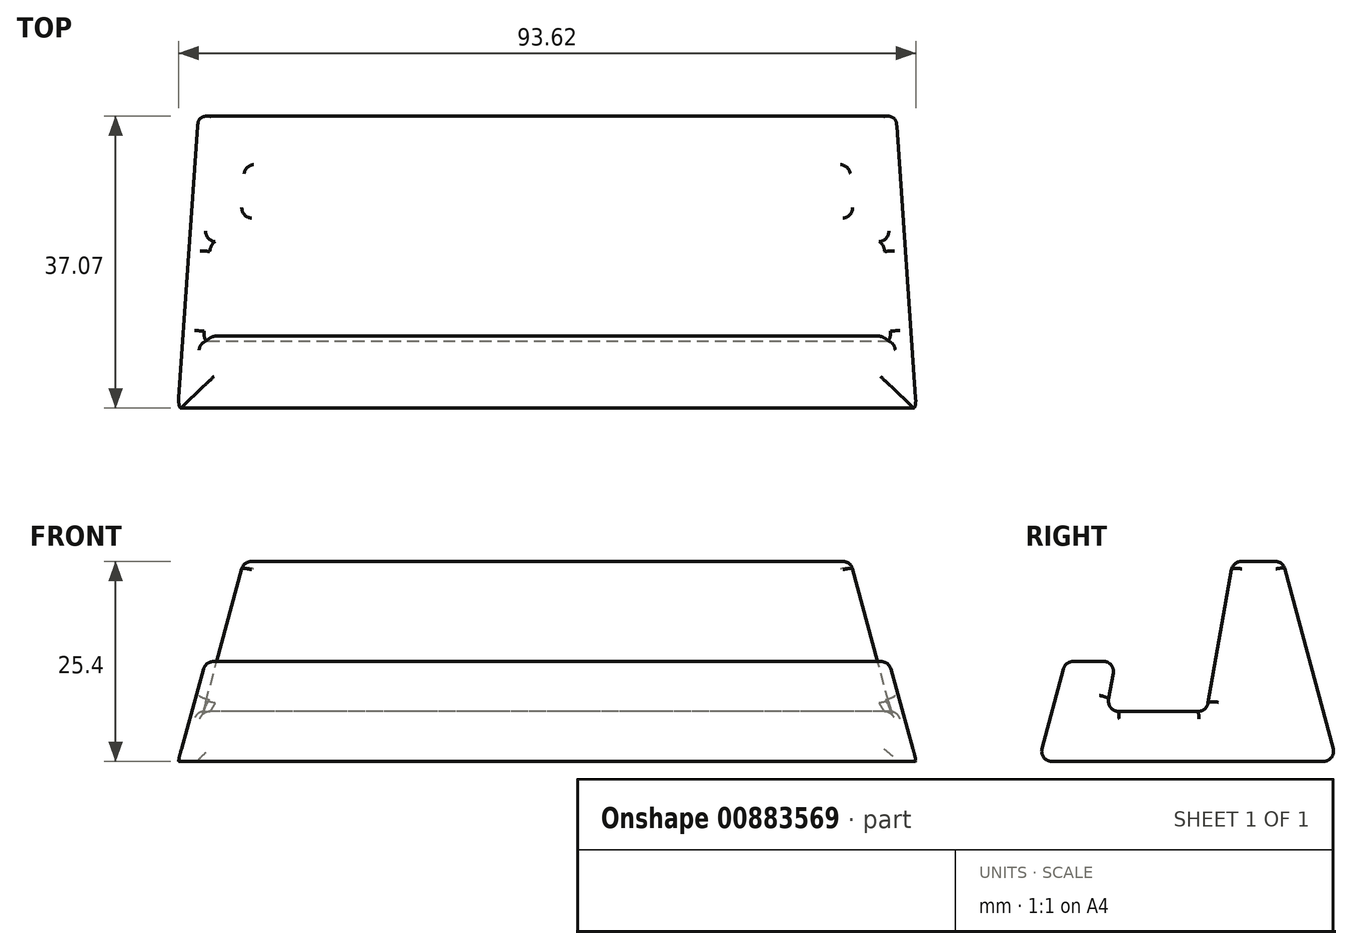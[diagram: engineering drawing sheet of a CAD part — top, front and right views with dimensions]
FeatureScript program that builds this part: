
annotation { "Feature Type Name" : "Feature", "Feature Type Description" : "" }
export const myFeature = defineFeature(function(context is Context, id is Id, definition is map)
    precondition{}
    {
        {
            var Q0;
            Q0=qCreatedBy(makeId("Right.planeOp"),FACE);
            var sketch = newSketch(context, id + "F0", { "sketchPlane" : qUnion([Q0])});
            skLineSegment(sketch, "E0", {"start": v(20.17, 0) * mm, "end": v(-17.68, 0) * mm});
            skLineSegment(sketch, "E1", {"start": v(-17.68, 0) * mm, "end": v(-14.28, 12.7) * mm});
            skLineSegment(sketch, "E2", {"start": v(-14.28, 12.7) * mm, "end": v(-7.93, 12.7) * mm});
            skLineSegment(sketch, "E3", {"start": v(-7.93, 12.7) * mm, "end": v(-9.05, 6.35) * mm});
            skLineSegment(sketch, "E4", {"start": v(-9.05, 6.35) * mm, "end": v(3.65, 6.35) * mm});
            skLineSegment(sketch, "E5", {"start": v(3.65, 6.35) * mm, "end": v(7.01, 25.4) * mm});
            skLineSegment(sketch, "E6", {"start": v(7.01, 25.4) * mm, "end": v(13.36, 25.4) * mm});
            skLineSegment(sketch, "E7", {"start": v(13.36, 25.4) * mm, "end": v(20.17, 0) * mm});
            skSolve(sketch);
        }
        {
            var Q0;
            Q0 = qSketchRegion(id + "F0", true);
            extrude(context, id + "F1", {"entities" : qUnion([Q0]), "endBound" : BoundingType.SYMMETRIC, "depth" : 50.8 * mm, "offsetDistance" : 25.4 * mm});
        }
        {
            var Q0;
            Q0=makeQuery(id+"F1.opExtrude","SWEPT_FACE",FACE,{"disambiguationData":[OSD([sQuery(id+"F0.wireOp",EDGE,"E1")])]});
            var sketch = newSketch(context, id + "F2", { "sketchPlane" : qUnion([Q0])});
            skLineSegment(sketch, "E8", {"start": v(21.51, -4.58) * mm, "end": v(12.7, 28.31) * mm});
            skLineSegment(sketch, "E9", {"start": v(12.7, 28.31) * mm, "end": v(12.7, 36.18) * mm});
            skLineSegment(sketch, "E10", {"start": v(12.7, 36.18) * mm, "end": v(48.13, 36.18) * mm});
            skLineSegment(sketch, "E11", {"start": v(48.13, 36.18) * mm, "end": v(48.13, -11.66) * mm});
            skLineSegment(sketch, "E12", {"start": v(48.13, -11.66) * mm, "end": v(22.1, -11.66) * mm});
            skLineSegment(sketch, "E13", {"start": v(22.1, -11.66) * mm, "end": v(21.51, -4.58) * mm});
            skSolve(sketch);
        }
        {
            var Q0;
            {var subQ0=sQuery(id+"F2.wireOp",EDGE,"E9");Q0=makeQuery(id+"F2.imprint","IMPRINT",FACE,{"disambiguationData":[TD([[makeQuery(id+"F2.imprint","IMPRINT",EDGE,{"derivedFrom":subQ0}),-1.0]])]});}
            var Q1;
            {var subQ1=sQuery(id+"F0.wireOp",EDGE,"E1");var subQ6=makeQuery(id+"F1.opExtrude","CAP_EDGE",EDGE,{"disambiguationData":[OSD([subQ1])],"isStart":false});Q1=makeQuery(id+"F2.imprint","IMPRINT",FACE,{"disambiguationData":[TD([[makeQuery(id+"F2.imprint","IMPRINT",EDGE,{"derivedFrom":subQ6}),1.0]])]});}
            extrude(context, id + "F3", {"entities" : qUnion([Q0, Q1]), "operationType" : NewBodyOperationType.REMOVE, "endBound" : BoundingType.THROUGH_ALL, "oppositeDirection" : true, "depth" : 25.4 * mm, "offsetDistance" : 25.4 * mm});
        }
        {
            var Q0;
            Q0=makeQuery(id+"F1.opExtrude","SWEPT_BODY",BODY,{"disambiguationData":[OSD([sQuery(id+"F0.wireOp",EDGE,"E0"),sQuery(id+"F0.wireOp",EDGE,"E1"),sQuery(id+"F0.wireOp",EDGE,"E2"),sQuery(id+"F0.wireOp",EDGE,"E3"),sQuery(id+"F0.wireOp",EDGE,"E4"),sQuery(id+"F0.wireOp",EDGE,"E5"),sQuery(id+"F0.wireOp",EDGE,"E6"),sQuery(id+"F0.wireOp",EDGE,"E7")])]});
            var Q1;
            Q1=makeQuery(id+"F1.opExtrude","CAP_FACE",FACE,{"disambiguationData":[OSD([sQuery(id+"F0.wireOp",EDGE,"E0"),sQuery(id+"F0.wireOp",EDGE,"E1"),sQuery(id+"F0.wireOp",EDGE,"E2"),sQuery(id+"F0.wireOp",EDGE,"E3"),sQuery(id+"F0.wireOp",EDGE,"E4"),sQuery(id+"F0.wireOp",EDGE,"E5"),sQuery(id+"F0.wireOp",EDGE,"E6"),sQuery(id+"F0.wireOp",EDGE,"E7")])],"isStart":true});
            mirror(context, id + "F4", {"operationType" : NewBodyOperationType.ADD, "entities" : qUnion([Q0]), "mirrorPlane" : qUnion([Q1])});
        }
        {
            var Q0;
            {var subQ0=makeQuery(id+"F1.opExtrude","SWEPT_EDGE",EDGE,{"disambiguationData":[OSD([sQuery(id+"F0.wireOp",EDGE,"E5"),sQuery(id+"F0.wireOp",EDGE,"E6")])]});Q0=makeQuery(id+"F4.boolean.opBoolean","MERGE",EDGE,{"derivedFrom":[subQ0,makeQuery(id+"F4.opPattern","COPY",EDGE,{"derivedFrom":subQ0,"instanceName":"1"})]});}
            var Q1;
            {var subQ0=makeQuery(id+"F1.opExtrude","SWEPT_EDGE",EDGE,{"disambiguationData":[OSD([sQuery(id+"F0.wireOp",EDGE,"E6"),sQuery(id+"F0.wireOp",EDGE,"E7")])]});Q1=makeQuery(id+"F4.boolean.opBoolean","MERGE",EDGE,{"derivedFrom":[subQ0,makeQuery(id+"F4.opPattern","COPY",EDGE,{"derivedFrom":subQ0,"instanceName":"1"})]});}
            var Q2;
            {var subQ0=makeQuery(id+"F1.opExtrude","SWEPT_EDGE",EDGE,{"disambiguationData":[OSD([sQuery(id+"F0.wireOp",EDGE,"E4"),sQuery(id+"F0.wireOp",EDGE,"E5")])]});Q2=makeQuery(id+"F4.boolean.opBoolean","MERGE",EDGE,{"derivedFrom":[subQ0,makeQuery(id+"F4.opPattern","COPY",EDGE,{"derivedFrom":subQ0,"instanceName":"1"})]});}
            var Q3;
            {var subQ0=makeQuery(id+"F1.opExtrude","SWEPT_EDGE",EDGE,{"disambiguationData":[OSD([sQuery(id+"F0.wireOp",EDGE,"E2"),sQuery(id+"F0.wireOp",EDGE,"E3")])]});Q3=makeQuery(id+"F4.boolean.opBoolean","MERGE",EDGE,{"derivedFrom":[subQ0,makeQuery(id+"F4.opPattern","COPY",EDGE,{"derivedFrom":subQ0,"instanceName":"1"})]});}
            var Q4;
            {var subQ0=makeQuery(id+"F1.opExtrude","SWEPT_EDGE",EDGE,{"disambiguationData":[OSD([sQuery(id+"F0.wireOp",EDGE,"E1"),sQuery(id+"F0.wireOp",EDGE,"E2")])]});Q4=makeQuery(id+"F4.boolean.opBoolean","MERGE",EDGE,{"derivedFrom":[subQ0,makeQuery(id+"F4.opPattern","COPY",EDGE,{"derivedFrom":subQ0,"instanceName":"1"})]});}
            var Q5;
            {var subQ0=makeQuery(id+"F1.opExtrude","SWEPT_EDGE",EDGE,{"disambiguationData":[OSD([sQuery(id+"F0.wireOp",EDGE,"E0"),sQuery(id+"F0.wireOp",EDGE,"E1")])]});Q5=makeQuery(id+"F4.boolean.opBoolean","MERGE",EDGE,{"derivedFrom":[subQ0,makeQuery(id+"F4.opPattern","COPY",EDGE,{"derivedFrom":subQ0,"instanceName":"1"})]});}
            var Q6;
            {var subQ0=makeQuery(id+"F1.opExtrude","SWEPT_EDGE",EDGE,{"disambiguationData":[OSD([sQuery(id+"F0.wireOp",EDGE,"E3"),sQuery(id+"F0.wireOp",EDGE,"E4")])]});Q6=makeQuery(id+"F4.boolean.opBoolean","MERGE",EDGE,{"derivedFrom":[subQ0,makeQuery(id+"F4.opPattern","COPY",EDGE,{"derivedFrom":subQ0,"instanceName":"1"})]});}
            var Q7;
            Q7=makeQuery(id+"F4.opPattern","COPY",EDGE,{"derivedFrom":makeQuery(id+"F3.boolean.opBoolean","INTERSECT",EDGE,{"derivedFrom":[makeQuery(id+"F1.opExtrude","SWEPT_FACE",FACE,{"disambiguationData":[OSD([sQuery(id+"F0.wireOp",EDGE,"E7")])]}),makeQuery(id+"F3.opExtrude","SWEPT_FACE",FACE,{"disambiguationData":[OSD([sQuery(id+"F2.wireOp",EDGE,"E8")])]})]}),"instanceName":"1"});
            var Q8;
            {var subQ0=makeQuery(id+"F1.opExtrude","SWEPT_EDGE",EDGE,{"disambiguationData":[OSD([sQuery(id+"F0.wireOp",EDGE,"E0"),sQuery(id+"F0.wireOp",EDGE,"E7")])]});Q8=makeQuery(id+"F4.boolean.opBoolean","MERGE",EDGE,{"derivedFrom":[subQ0,makeQuery(id+"F4.opPattern","COPY",EDGE,{"derivedFrom":subQ0,"instanceName":"1"})]});}
            var Q9;
            Q9=makeQuery(id+"F4.opPattern","COPY",EDGE,{"derivedFrom":makeQuery(id+"F3.boolean.opBoolean","COPY",EDGE,{"derivedFrom":makeQuery(id+"F3.opExtrude","CAP_EDGE",EDGE,{"disambiguationData":[OSD([sQuery(id+"F2.wireOp",EDGE,"E8")])],"isStart":true})}),"instanceName":"1"});
            var Q10;
            Q10=makeQuery(id+"F4.opPattern","COPY",EDGE,{"derivedFrom":makeQuery(id+"F3.boolean.opBoolean","INTERSECT",EDGE,{"derivedFrom":[makeQuery(id+"F1.opExtrude","SWEPT_FACE",FACE,{"disambiguationData":[OSD([sQuery(id+"F0.wireOp",EDGE,"E5")])]}),makeQuery(id+"F3.opExtrude","SWEPT_FACE",FACE,{"disambiguationData":[OSD([sQuery(id+"F2.wireOp",EDGE,"E8")])]})]}),"instanceName":"1"});
            var Q11;
            Q11=makeQuery(id+"F4.opPattern","COPY",EDGE,{"derivedFrom":makeQuery(id+"F3.boolean.opBoolean","INTERSECT",EDGE,{"derivedFrom":[makeQuery(id+"F1.opExtrude","SWEPT_FACE",FACE,{"disambiguationData":[OSD([sQuery(id+"F0.wireOp",EDGE,"E6")])]}),makeQuery(id+"F3.opExtrude","SWEPT_FACE",FACE,{"disambiguationData":[OSD([sQuery(id+"F2.wireOp",EDGE,"E8")])]})]}),"instanceName":"1"});
            var Q12;
            Q12=makeQuery(id+"F4.opPattern","COPY",EDGE,{"derivedFrom":makeQuery(id+"F3.boolean.opBoolean","INTERSECT",EDGE,{"derivedFrom":[makeQuery(id+"F1.opExtrude","SWEPT_FACE",FACE,{"disambiguationData":[OSD([sQuery(id+"F0.wireOp",EDGE,"E2")])]}),makeQuery(id+"F3.opExtrude","SWEPT_FACE",FACE,{"disambiguationData":[OSD([sQuery(id+"F2.wireOp",EDGE,"E8")])]})]}),"instanceName":"1"});
            var Q13;
            Q13=makeQuery(id+"F4.opPattern","COPY",EDGE,{"derivedFrom":makeQuery(id+"F3.boolean.opBoolean","INTERSECT",EDGE,{"derivedFrom":[makeQuery(id+"F1.opExtrude","SWEPT_FACE",FACE,{"disambiguationData":[OSD([sQuery(id+"F0.wireOp",EDGE,"E3")])]}),makeQuery(id+"F3.opExtrude","SWEPT_FACE",FACE,{"disambiguationData":[OSD([sQuery(id+"F2.wireOp",EDGE,"E8")])]})]}),"instanceName":"1"});
            var Q14;
            Q14=makeQuery(id+"F3.boolean.opBoolean","COPY",EDGE,{"derivedFrom":makeQuery(id+"F3.opExtrude","CAP_EDGE",EDGE,{"disambiguationData":[OSD([sQuery(id+"F2.wireOp",EDGE,"E8")])],"isStart":true})});
            var Q15;
            Q15=makeQuery(id+"F3.boolean.opBoolean","INTERSECT",EDGE,{"derivedFrom":[makeQuery(id+"F1.opExtrude","SWEPT_FACE",FACE,{"disambiguationData":[OSD([sQuery(id+"F0.wireOp",EDGE,"E2")])]}),makeQuery(id+"F3.opExtrude","SWEPT_FACE",FACE,{"disambiguationData":[OSD([sQuery(id+"F2.wireOp",EDGE,"E8")])]})]});
            var Q16;
            Q16=makeQuery(id+"F3.boolean.opBoolean","INTERSECT",EDGE,{"derivedFrom":[makeQuery(id+"F1.opExtrude","SWEPT_FACE",FACE,{"disambiguationData":[OSD([sQuery(id+"F0.wireOp",EDGE,"E3")])]}),makeQuery(id+"F3.opExtrude","SWEPT_FACE",FACE,{"disambiguationData":[OSD([sQuery(id+"F2.wireOp",EDGE,"E8")])]})]});
            var Q17;
            Q17=makeQuery(id+"F3.boolean.opBoolean","INTERSECT",EDGE,{"derivedFrom":[makeQuery(id+"F1.opExtrude","SWEPT_FACE",FACE,{"disambiguationData":[OSD([sQuery(id+"F0.wireOp",EDGE,"E4")])]}),makeQuery(id+"F3.opExtrude","SWEPT_FACE",FACE,{"disambiguationData":[OSD([sQuery(id+"F2.wireOp",EDGE,"E8")])]})]});
            var Q18;
            Q18=makeQuery(id+"F3.boolean.opBoolean","INTERSECT",EDGE,{"derivedFrom":[makeQuery(id+"F1.opExtrude","SWEPT_FACE",FACE,{"disambiguationData":[OSD([sQuery(id+"F0.wireOp",EDGE,"E5")])]}),makeQuery(id+"F3.opExtrude","SWEPT_FACE",FACE,{"disambiguationData":[OSD([sQuery(id+"F2.wireOp",EDGE,"E8")])]})]});
            var Q19;
            Q19=makeQuery(id+"F3.boolean.opBoolean","INTERSECT",EDGE,{"derivedFrom":[makeQuery(id+"F1.opExtrude","SWEPT_FACE",FACE,{"disambiguationData":[OSD([sQuery(id+"F0.wireOp",EDGE,"E7")])]}),makeQuery(id+"F3.opExtrude","SWEPT_FACE",FACE,{"disambiguationData":[OSD([sQuery(id+"F2.wireOp",EDGE,"E8")])]})]});
            var Q20;
            Q20=makeQuery(id+"F3.boolean.opBoolean","INTERSECT",EDGE,{"derivedFrom":[makeQuery(id+"F1.opExtrude","SWEPT_FACE",FACE,{"disambiguationData":[OSD([sQuery(id+"F0.wireOp",EDGE,"E6")])]}),makeQuery(id+"F3.opExtrude","SWEPT_FACE",FACE,{"disambiguationData":[OSD([sQuery(id+"F2.wireOp",EDGE,"E8")])]})]});
            var Q21;
            Q21=makeQuery(id+"F4.opPattern","COPY",EDGE,{"derivedFrom":makeQuery(id+"F3.boolean.opBoolean","INTERSECT",EDGE,{"derivedFrom":[makeQuery(id+"F1.opExtrude","SWEPT_FACE",FACE,{"disambiguationData":[OSD([sQuery(id+"F0.wireOp",EDGE,"E4")])]}),makeQuery(id+"F3.opExtrude","SWEPT_FACE",FACE,{"disambiguationData":[OSD([sQuery(id+"F2.wireOp",EDGE,"E8")])]})]}),"instanceName":"1"});
            fillet(context, id + "F5", {"entities" : qUnion([Q0, Q1, Q2, Q3, Q4, Q5, Q6, Q7, Q8, Q9, Q10, Q11, Q12, Q13, Q14, Q15, Q16, Q17, Q18, Q19, Q20, Q21]), "radius" : 1.27 * mm, "tangentPropagation" : true, "allowEdgeOverflow" : false});
        }
    });
